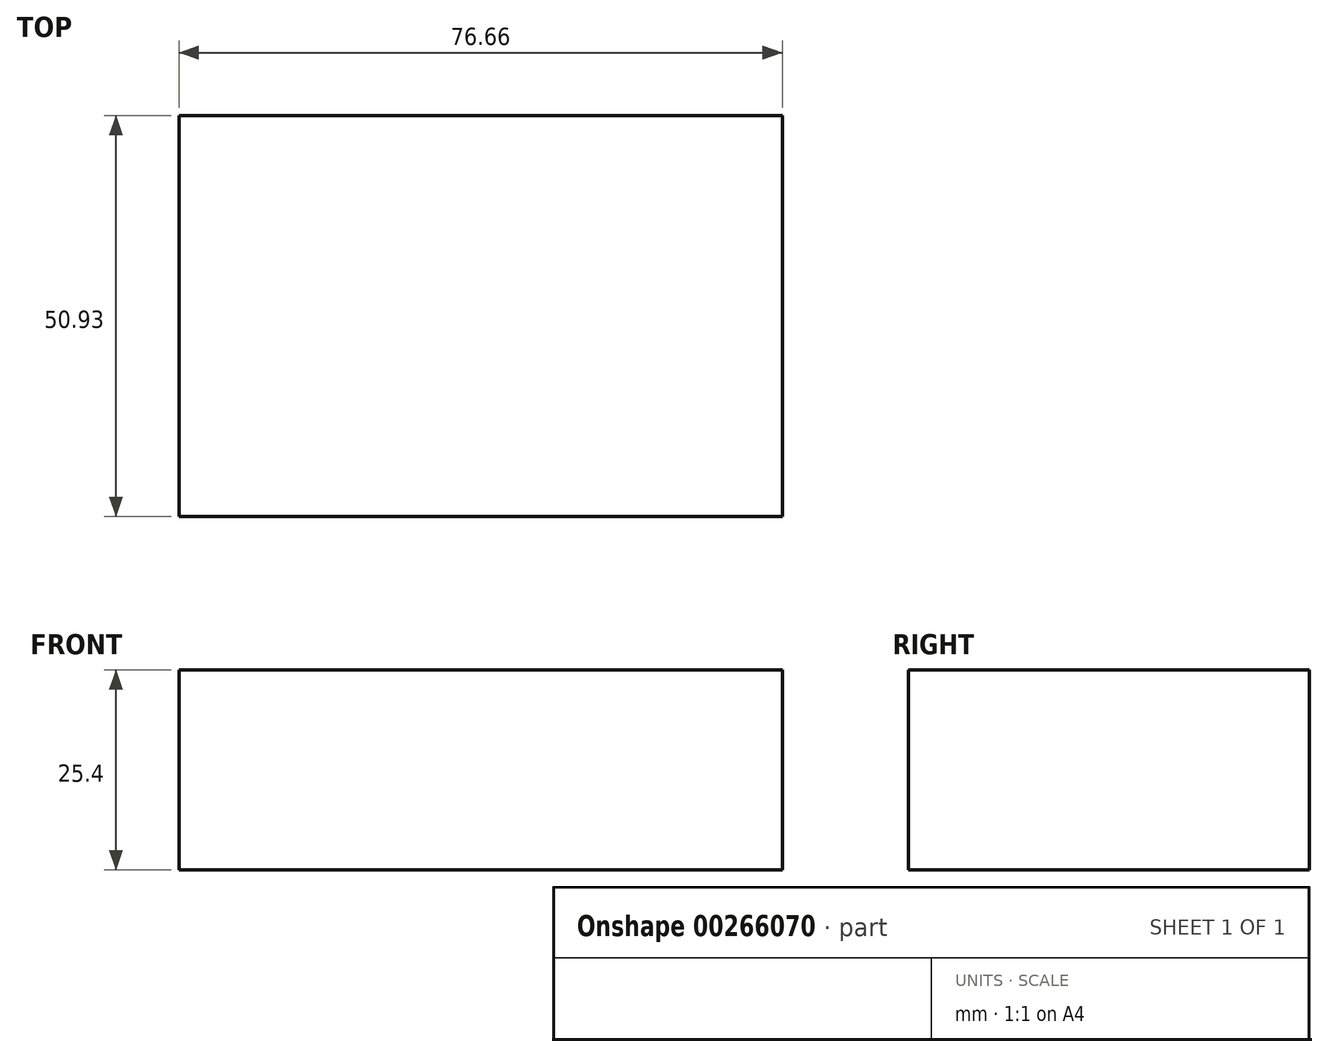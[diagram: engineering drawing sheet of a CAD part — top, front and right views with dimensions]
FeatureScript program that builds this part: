
annotation { "Feature Type Name" : "Feature", "Feature Type Description" : "" }
export const myFeature = defineFeature(function(context is Context, id is Id, definition is map)
    precondition{}
    {
        {
            var Q0;
            Q0=qCreatedBy(makeId("Top.planeOp"),FACE);
            var sketch = newSketch(context, id + "F0", { "sketchPlane" : qUnion([Q0])});
            skLineSegment(sketch, "E0.bottom", {"start": v(40.08, 25.87) * mm, "end": v(-40.08, 25.87) * mm});
            skLineSegment(sketch, "E0.top", {"start": v(46.43, -25.87) * mm, "end": v(-46.43, -25.87) * mm});
            skLineSegment(sketch, "E0.left", {"start": v(46.43, 19.52) * mm, "end": v(46.43, -25.87) * mm});
            skLineSegment(sketch, "E0.right", {"start": v(-46.43, 19.52) * mm, "end": v(-46.43, -25.87) * mm});
            skPoint(sketch, "E0.middle", {"position": v(0, 0) * mm});
            skPoint(sketch, "E1.visualSharp", {"position": v(-46.43, 25.87) * mm});
            skArc(sketch, "E1.filletArc", {"start": v(-40.08, 25.87) * mm, "mid": v(-44.57, 24) * mm, "end": v(-46.43, 19.52) * mm});
            skPoint(sketch, "E2.visualSharp", {"position": v(46.43, 25.87) * mm});
            skArc(sketch, "E2.filletArc", {"start": v(46.43, 19.52) * mm, "mid": v(44.57, 24) * mm, "end": v(40.08, 25.87) * mm});
            skSolve(sketch);
        }
        {
            var Q0;
            Q0=makeQuery(id+"F0.imprint","IMPRINT",FACE,{"disambiguationData":[TD([[makeQuery(id+"F0.imprint","IMPRINT",EDGE,{"derivedFrom":sQuery(id+"F0.wireOp",EDGE,"E0.bottom")}),1.0]])]});
            extrude(context, id + "F1", {"entities" : qUnion([Q0]), "depth" : 25.4 * mm});
        }
        {
            var Q0;
            Q0=qCreatedBy(makeId("Top.planeOp"),FACE);
            var sketch = newSketch(context, id + "F2", { "sketchPlane" : qUnion([Q0])});
            skCircle(sketch, "E3", {"center": v(0, 34.71) * mm, "radius": 24.8 * mm});
            skSolve(sketch);
        }
        {
            var Q0;
            Q0 = qSketchRegion(id + "F2", true);
            extrude(context, id + "F3", {"entities" : qUnion([Q0]), "operationType" : NewBodyOperationType.REMOVE, "oppositeDirection" : true, "depth" : 25.4 * mm, "hasSecondDirection" : true, "secondDirectionOppositeDirection" : false, "secondDirectionDepth" : 25.4 * mm});
        }
        {
            var Q0;
            Q0=qCreatedBy(makeId("Top.planeOp"),FACE);
            var sketch = newSketch(context, id + "F4", { "sketchPlane" : qUnion([Q0])});
            skLineSegment(sketch, "E4.bottom", {"start": v(-38.06, -25.33) * mm, "end": v(38.6, -25.33) * mm});
            skLineSegment(sketch, "E4.top", {"start": v(-38.06, -8.98) * mm, "end": v(38.6, -8.98) * mm});
            skLineSegment(sketch, "E4.left", {"start": v(-38.06, -25.33) * mm, "end": v(-38.06, -8.98) * mm});
            skLineSegment(sketch, "E4.right", {"start": v(38.6, -25.33) * mm, "end": v(38.6, -8.98) * mm});
            skLineSegment(sketch, "E5.bottom", {"start": v(-38.06, 25.6) * mm, "end": v(38.6, 25.6) * mm});
            skLineSegment(sketch, "E5.left", {"start": v(-38.06, 25.6) * mm, "end": v(-38.06, -8.98) * mm});
            skLineSegment(sketch, "E5.right", {"start": v(38.6, 25.6) * mm, "end": v(38.6, -8.98) * mm});
            skSolve(sketch);
        }
        {
            var Q0;
            Q0=makeQuery(id+"F1.opExtrude","CAP_FACE",FACE,{"disambiguationData":[OSD([sQuery(id+"F0.wireOp",EDGE,"E0.bottom"),sQuery(id+"F0.wireOp",EDGE,"E0.top"),sQuery(id+"F0.wireOp",EDGE,"E0.left"),sQuery(id+"F0.wireOp",EDGE,"E0.right"),sQuery(id+"F0.wireOp",EDGE,"E1.filletArc"),sQuery(id+"F0.wireOp",EDGE,"E2.filletArc")])],"isStart":false});
            extrude(context, id + "F5", {"entities" : qUnion([Q0]), "operationType" : NewBodyOperationType.REMOVE, "oppositeDirection" : true, "depth" : 50.8 * mm});
        }
        {
            var Q0;
            Q0 = qSketchRegion(id + "F4", true);
            extrude(context, id + "F6", {"entities" : qUnion([Q0]), "depth" : 25.4 * mm});
        }
    });
